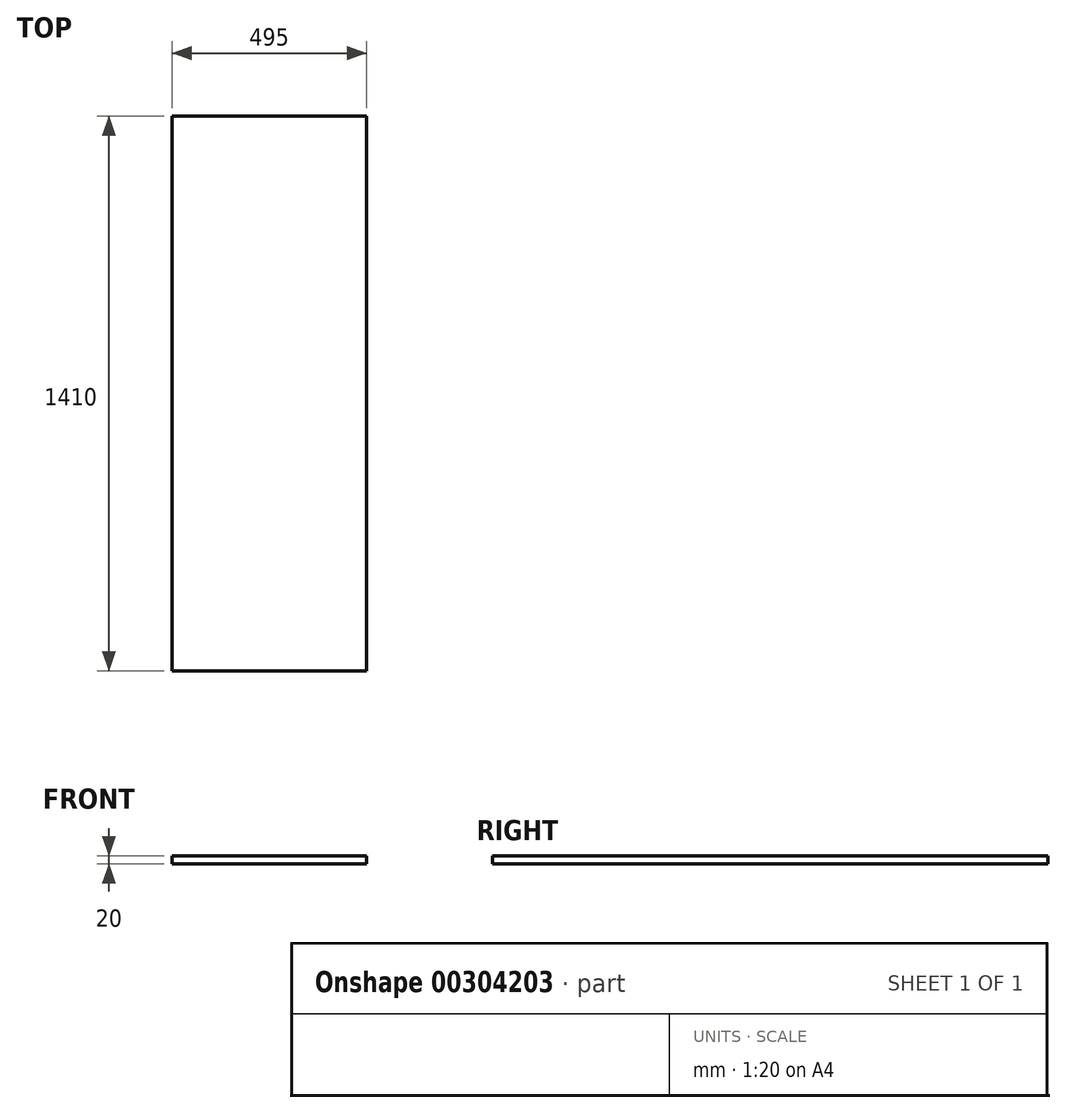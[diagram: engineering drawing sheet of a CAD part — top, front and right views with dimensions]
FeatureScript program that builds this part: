
annotation { "Feature Type Name" : "Feature", "Feature Type Description" : "" }
export const myFeature = defineFeature(function(context is Context, id is Id, definition is map)
    precondition{}
    {
        {
            var Q0;
            Q0=qCreatedBy(makeId("Right.planeOp"),FACE);
            var sketch = newSketch(context, id + "F0", { "sketchPlane" : qUnion([Q0])});
            skLineSegment(sketch, "E0.bottom", {"start": v(0, 20) * mm, "end": v(1410, 20) * mm});
            skLineSegment(sketch, "E0.top", {"start": v(0, 0) * mm, "end": v(1410, 0) * mm});
            skLineSegment(sketch, "E0.left", {"start": v(0, 20) * mm, "end": v(0, 0) * mm});
            skLineSegment(sketch, "E0.right", {"start": v(1410, 20) * mm, "end": v(1410, 0) * mm});
            skSolve(sketch);
        }
        {
            var Q0;
            Q0 = qSketchRegion(id + "F0", true);
            extrude(context, id + "F1", {"entities" : qUnion([Q0]), "depth" : 495 * mm});
        }
    });
